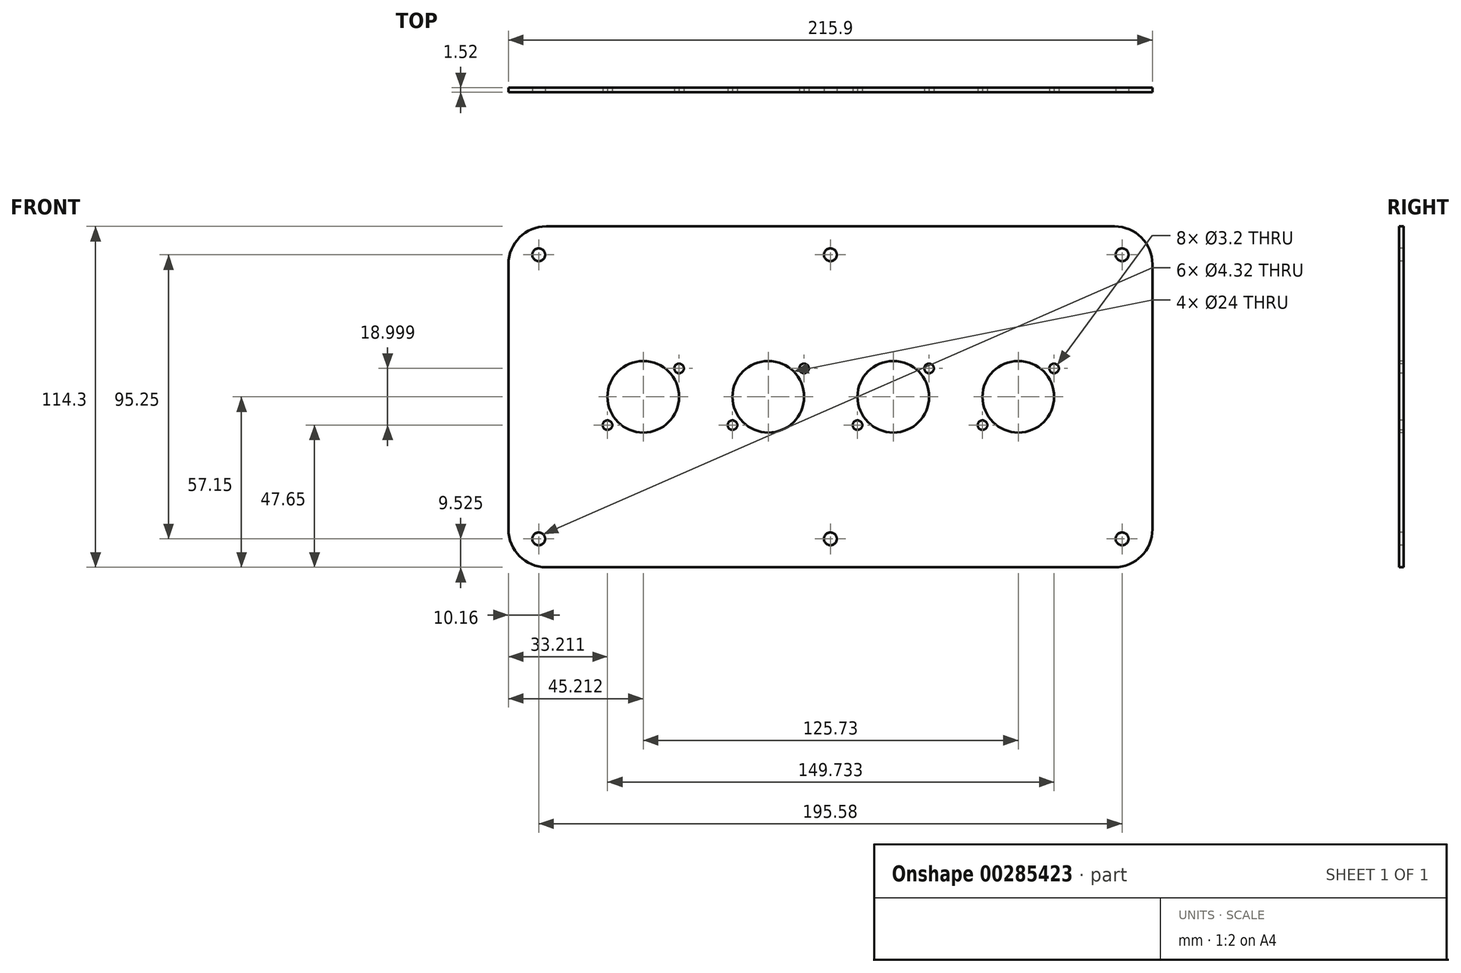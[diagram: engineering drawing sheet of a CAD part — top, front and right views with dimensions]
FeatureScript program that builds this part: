
annotation { "Feature Type Name" : "Feature", "Feature Type Description" : "" }
export const myFeature = defineFeature(function(context is Context, id is Id, definition is map)
    precondition{}
    {
        {
            var Q0;
            Q0=qCreatedBy(makeId("Front.planeOp"),FACE);
            var sketch = newSketch(context, id + "F0", { "sketchPlane" : qUnion([Q0])});
            skLineSegment(sketch, "E0.bottom", {"start": v(33.27, -22.23) * mm, "end": v(182.63, -22.23) * mm, "construction": true});
            skLineSegment(sketch, "E0.top", {"start": v(33.27, -92.08) * mm, "end": v(182.63, -92.08) * mm, "construction": true});
            skLineSegment(sketch, "E0.left", {"start": v(24.13, -31.37) * mm, "end": v(24.13, -82.93) * mm, "construction": true});
            skLineSegment(sketch, "E0.right", {"start": v(191.77, -31.37) * mm, "end": v(191.77, -82.93) * mm, "construction": true});
            skPoint(sketch, "E1.visualSharp", {"position": v(24.13, -22.23) * mm});
            skArc(sketch, "E1.filletArc", {"start": v(33.27, -22.23) * mm, "mid": v(26.8, -24.9) * mm, "end": v(24.13, -31.37) * mm, "construction": true});
            skPoint(sketch, "E2.visualSharp", {"position": v(191.77, -22.23) * mm});
            skArc(sketch, "E2.filletArc", {"start": v(191.77, -31.37) * mm, "mid": v(189.1, -24.9) * mm, "end": v(182.63, -22.22) * mm, "construction": true});
            skPoint(sketch, "E3.visualSharp", {"position": v(191.77, -92.08) * mm});
            skArc(sketch, "E3.filletArc", {"start": v(182.63, -92.08) * mm, "mid": v(189.1, -89.4) * mm, "end": v(191.77, -82.93) * mm, "construction": true});
            skPoint(sketch, "E4.visualSharp", {"position": v(24.13, -92.08) * mm});
            skArc(sketch, "E4.filletArc", {"start": v(24.13, -82.93) * mm, "mid": v(26.8, -89.4) * mm, "end": v(33.27, -92.07) * mm, "construction": true});
            skLineSegment(sketch, "E5.bottom", {"start": v(12.7, 0) * mm, "end": v(203.2, 0) * mm});
            skLineSegment(sketch, "E5.top", {"start": v(12.7, -114.3) * mm, "end": v(203.2, -114.3) * mm});
            skLineSegment(sketch, "E5.left", {"start": v(0, -12.7) * mm, "end": v(0, -101.6) * mm});
            skLineSegment(sketch, "E5.right", {"start": v(215.9, -12.7) * mm, "end": v(215.9, -101.6) * mm});
            skPoint(sketch, "E6.visualSharp", {"position": v(0, 0) * mm});
            skArc(sketch, "E6.filletArc", {"start": v(12.7, 0) * mm, "mid": v(3.72, -3.72) * mm, "end": v(0, -12.7) * mm});
            skPoint(sketch, "E7.visualSharp", {"position": v(215.9, 0) * mm});
            skArc(sketch, "E7.filletArc", {"start": v(215.9, -12.7) * mm, "mid": v(212.18, -3.72) * mm, "end": v(203.2, 0) * mm});
            skPoint(sketch, "E8.visualSharp", {"position": v(215.9, -114.3) * mm});
            skArc(sketch, "E8.filletArc", {"start": v(203.2, -114.3) * mm, "mid": v(212.18, -110.58) * mm, "end": v(215.9, -101.6) * mm});
            skPoint(sketch, "E9.visualSharp", {"position": v(0, -114.3) * mm});
            skArc(sketch, "E9.filletArc", {"start": v(0, -101.6) * mm, "mid": v(3.72, -110.58) * mm, "end": v(12.7, -114.3) * mm});
            skLineSegment(sketch, "E10", {"start": v(107.95, 0) * mm, "end": v(107.95, -114.3) * mm, "construction": true});
            skLineSegment(sketch, "E11", {"start": v(0, -57.15) * mm, "end": v(215.9, -57.15) * mm, "construction": true});
            skPoint(sketch, "E12", {"position": v(107.95, -22.23) * mm});
            skPoint(sketch, "E13", {"position": v(191.77, -57.15) * mm});
            skPoint(sketch, "E14", {"position": v(10.16, -9.52) * mm});
            skPoint(sketch, "E15", {"position": v(107.95, -9.52) * mm});
            skPoint(sketch, "E16", {"position": v(205.74, -9.52) * mm});
            skPoint(sketch, "E17", {"position": v(205.74, -104.78) * mm});
            skPoint(sketch, "E18", {"position": v(107.95, -104.78) * mm});
            skPoint(sketch, "E19", {"position": v(10.16, -104.78) * mm});
            skLineSegment(sketch, "E20", {"start": v(10.16, -9.52) * mm, "end": v(10.16, -104.78) * mm, "construction": true});
            skSolve(sketch);
        }
        {
            var Q0;
            Q0=makeQuery(id+"F0.imprint","IMPRINT",FACE,{"disambiguationData":[TD([[makeQuery(id+"F0.imprint","IMPRINT",EDGE,{"derivedFrom":sQuery(id+"F0.wireOp",EDGE,"E5.bottom")}),-1.0]])]});
            extrude(context, id + "F1", {"entities" : qUnion([Q0]), "depth" : 1.52 * mm});
        }
        {
            var Q0;
            Q0=makeQuery(id+"F1.opExtrude","CAP_FACE",FACE,{"disambiguationData":[OSD([sQuery(id+"F0.wireOp",EDGE,"E5.bottom"),sQuery(id+"F0.wireOp",EDGE,"E5.top"),sQuery(id+"F0.wireOp",EDGE,"E5.left"),sQuery(id+"F0.wireOp",EDGE,"E5.right"),sQuery(id+"F0.wireOp",EDGE,"E6.filletArc"),sQuery(id+"F0.wireOp",EDGE,"E7.filletArc"),sQuery(id+"F0.wireOp",EDGE,"E8.filletArc"),sQuery(id+"F0.wireOp",EDGE,"E9.filletArc")])],"isStart":false});
            var sketch = newSketch(context, id + "F2", { "sketchPlane" : qUnion([Q0])});
            skCircle(sketch, "E21", {"center": v(45.21, -57.15) * mm, "radius": 12 * mm});
            skCircle(sketch, "E22.MirrorC", {"center": v(33.21, -66.65) * mm, "radius": 1.6 * mm});
            skCircle(sketch, "E23.MirrorC", {"center": v(57.21, -47.65) * mm, "radius": 1.6 * mm});
            skLineSegment(sketch, "E24.bottom", {"start": v(29.72, -66.45) * mm, "end": v(29.72, -47.85) * mm, "construction": true});
            skLineSegment(sketch, "E24.top", {"start": v(60.7, -66.45) * mm, "end": v(60.7, -47.85) * mm, "construction": true});
            skLineSegment(sketch, "E24.left", {"start": v(33.22, -69.95) * mm, "end": v(57.2, -69.95) * mm, "construction": true});
            skLineSegment(sketch, "E24.right", {"start": v(33.22, -44.35) * mm, "end": v(57.2, -44.35) * mm, "construction": true});
            skPoint(sketch, "E25.visualSharp", {"position": v(29.72, -69.95) * mm});
            skArc(sketch, "E25.filletArc", {"start": v(29.72, -66.45) * mm, "mid": v(30.74, -68.93) * mm, "end": v(33.22, -69.95) * mm, "construction": true});
            skPoint(sketch, "E26.visualSharp", {"position": v(29.72, -44.35) * mm});
            skArc(sketch, "E26.filletArc", {"start": v(33.22, -44.35) * mm, "mid": v(30.74, -45.37) * mm, "end": v(29.72, -47.85) * mm, "construction": true});
            skPoint(sketch, "E27.visualSharp", {"position": v(60.7, -69.95) * mm});
            skArc(sketch, "E27.filletArc", {"start": v(57.2, -69.95) * mm, "mid": v(59.68, -68.93) * mm, "end": v(60.7, -66.45) * mm, "construction": true});
            skPoint(sketch, "E28.visualSharp", {"position": v(60.7, -44.35) * mm});
            skArc(sketch, "E28.filletArc", {"start": v(60.7, -47.85) * mm, "mid": v(59.68, -45.37) * mm, "end": v(57.2, -44.35) * mm, "construction": true});
            skLineSegment(sketch, "E29.bottom", {"start": v(64.81, -71.08) * mm, "end": v(64.81, -43.23) * mm, "construction": true});
            skLineSegment(sketch, "E29.top", {"start": v(25.61, -71.08) * mm, "end": v(25.61, -43.23) * mm, "construction": true});
            skLineSegment(sketch, "E29.left", {"start": v(61.64, -74.25) * mm, "end": v(28.79, -74.25) * mm, "construction": true});
            skLineSegment(sketch, "E29.right", {"start": v(61.64, -40.05) * mm, "end": v(28.79, -40.05) * mm, "construction": true});
            skCircle(sketch, "E30", {"center": v(45.21, -57.15) * mm, "radius": 11.8 * mm, "construction": true});
            skLineSegment(sketch, "E31", {"start": v(25.61, -57.15) * mm, "end": v(64.81, -57.15) * mm, "construction": true});
            skLineSegment(sketch, "E32", {"start": v(45.21, -40.05) * mm, "end": v(45.21, -74.25) * mm, "construction": true});
            skCircle(sketch, "E33", {"center": v(33.22, -66.65) * mm, "radius": 1.55 * mm, "construction": true});
            skCircle(sketch, "E34", {"center": v(57.2, -47.65) * mm, "radius": 1.55 * mm, "construction": true});
            skPoint(sketch, "E35.visualSharp", {"position": v(25.61, -74.25) * mm});
            skArc(sketch, "E35.filletArc", {"start": v(25.61, -71.08) * mm, "mid": v(26.54, -73.32) * mm, "end": v(28.79, -74.25) * mm, "construction": true});
            skPoint(sketch, "E36.visualSharp", {"position": v(25.61, -40.05) * mm});
            skArc(sketch, "E36.filletArc", {"start": v(28.79, -40.05) * mm, "mid": v(26.54, -40.98) * mm, "end": v(25.61, -43.23) * mm, "construction": true});
            skPoint(sketch, "E37.visualSharp", {"position": v(64.81, -40.05) * mm});
            skArc(sketch, "E37.filletArc", {"start": v(64.81, -43.23) * mm, "mid": v(63.88, -40.98) * mm, "end": v(61.64, -40.05) * mm, "construction": true});
            skPoint(sketch, "E38.visualSharp", {"position": v(64.81, -74.25) * mm});
            skArc(sketch, "E38.filletArc", {"start": v(61.64, -74.25) * mm, "mid": v(63.88, -73.32) * mm, "end": v(64.81, -71.08) * mm, "construction": true});
            skLineSegment(sketch, "E39", {"start": v(0, -57.15) * mm, "end": v(215.9, -57.15) * mm, "construction": true});
            skLineSegment(sketch, "E40.1.0.0", {"start": v(106.72, -71.08) * mm, "end": v(106.72, -43.23) * mm, "construction": true});
            skLineSegment(sketch, "E40.1.0.1", {"start": v(67.52, -71.08) * mm, "end": v(67.52, -43.23) * mm, "construction": true});
            skPoint(sketch, "E40.1.0.2", {"position": v(102.62, -44.35) * mm});
            skPoint(sketch, "E40.1.0.3", {"position": v(71.63, -69.95) * mm});
            skCircle(sketch, "E40.1.0.4", {"center": v(75.13, -66.65) * mm, "radius": 1.55 * mm, "construction": true});
            skCircle(sketch, "E40.1.0.5", {"center": v(99.12, -47.65) * mm, "radius": 1.6 * mm});
            skCircle(sketch, "E40.1.0.6", {"center": v(99.11, -47.65) * mm, "radius": 1.55 * mm, "construction": true});
            skPoint(sketch, "E40.1.0.7", {"position": v(106.72, -40.05) * mm});
            skPoint(sketch, "E40.1.0.8", {"position": v(102.62, -69.95) * mm});
            skPoint(sketch, "E40.1.0.9", {"position": v(67.52, -40.05) * mm});
            skCircle(sketch, "E40.1.0.10", {"center": v(87.12, -57.15) * mm, "radius": 11.8 * mm, "construction": true});
            skCircle(sketch, "E40.1.0.11", {"center": v(87.12, -57.15) * mm, "radius": 12 * mm});
            skLineSegment(sketch, "E40.1.0.12", {"start": v(75.13, -69.95) * mm, "end": v(99.12, -69.95) * mm, "construction": true});
            skLineSegment(sketch, "E40.1.0.13", {"start": v(103.55, -74.25) * mm, "end": v(70.7, -74.25) * mm, "construction": true});
            skLineSegment(sketch, "E40.1.0.14", {"start": v(75.13, -44.35) * mm, "end": v(99.12, -44.35) * mm, "construction": true});
            skLineSegment(sketch, "E40.1.0.15", {"start": v(103.55, -40.05) * mm, "end": v(70.7, -40.05) * mm, "construction": true});
            skLineSegment(sketch, "E40.1.0.16", {"start": v(71.63, -66.45) * mm, "end": v(71.63, -47.85) * mm, "construction": true});
            skLineSegment(sketch, "E40.1.0.17", {"start": v(102.62, -66.45) * mm, "end": v(102.62, -47.85) * mm, "construction": true});
            skPoint(sketch, "E40.1.0.18", {"position": v(67.52, -74.25) * mm});
            skPoint(sketch, "E40.1.0.19", {"position": v(106.72, -74.25) * mm});
            skCircle(sketch, "E40.1.0.20", {"center": v(75.12, -66.65) * mm, "radius": 1.6 * mm});
            skLineSegment(sketch, "E40.1.0.21", {"start": v(87.12, -40.05) * mm, "end": v(87.12, -74.25) * mm, "construction": true});
            skPoint(sketch, "E40.1.0.22", {"position": v(71.63, -44.35) * mm});
            skLineSegment(sketch, "E40.1.0.23", {"start": v(41.9, -57.15) * mm, "end": v(257.8, -57.15) * mm, "construction": true});
            skArc(sketch, "E40.1.0.24", {"start": v(103.55, -74.25) * mm, "mid": v(105.8, -73.32) * mm, "end": v(106.72, -71.08) * mm, "construction": true});
            skArc(sketch, "E40.1.0.25", {"start": v(102.62, -47.85) * mm, "mid": v(101.6, -45.37) * mm, "end": v(99.12, -44.35) * mm, "construction": true});
            skArc(sketch, "E40.1.0.26", {"start": v(99.12, -69.95) * mm, "mid": v(101.6, -68.93) * mm, "end": v(102.62, -66.45) * mm, "construction": true});
            skArc(sketch, "E40.1.0.27", {"start": v(75.13, -44.35) * mm, "mid": v(72.65, -45.37) * mm, "end": v(71.63, -47.85) * mm, "construction": true});
            skArc(sketch, "E40.1.0.28", {"start": v(67.52, -71.08) * mm, "mid": v(68.45, -73.32) * mm, "end": v(70.7, -74.25) * mm, "construction": true});
            skArc(sketch, "E40.1.0.29", {"start": v(71.63, -66.45) * mm, "mid": v(72.65, -68.93) * mm, "end": v(75.13, -69.95) * mm, "construction": true});
            skLineSegment(sketch, "E40.1.0.30", {"start": v(67.52, -57.15) * mm, "end": v(106.72, -57.15) * mm, "construction": true});
            skArc(sketch, "E40.1.0.31", {"start": v(106.72, -43.23) * mm, "mid": v(105.8, -40.98) * mm, "end": v(103.55, -40.05) * mm, "construction": true});
            skArc(sketch, "E40.1.0.32", {"start": v(70.7, -40.05) * mm, "mid": v(68.45, -40.98) * mm, "end": v(67.52, -43.23) * mm, "construction": true});
            skLineSegment(sketch, "E40.2.0.0", {"start": v(148.63, -71.08) * mm, "end": v(148.63, -43.23) * mm, "construction": true});
            skLineSegment(sketch, "E40.2.0.1", {"start": v(109.43, -71.08) * mm, "end": v(109.43, -43.23) * mm, "construction": true});
            skPoint(sketch, "E40.2.0.2", {"position": v(144.53, -44.35) * mm});
            skPoint(sketch, "E40.2.0.3", {"position": v(113.54, -69.95) * mm});
            skCircle(sketch, "E40.2.0.4", {"center": v(117.04, -66.65) * mm, "radius": 1.55 * mm, "construction": true});
            skCircle(sketch, "E40.2.0.5", {"center": v(141.03, -47.65) * mm, "radius": 1.6 * mm});
            skCircle(sketch, "E40.2.0.6", {"center": v(141.02, -47.65) * mm, "radius": 1.55 * mm, "construction": true});
            skPoint(sketch, "E40.2.0.7", {"position": v(148.63, -40.05) * mm});
            skPoint(sketch, "E40.2.0.8", {"position": v(144.53, -69.95) * mm});
            skPoint(sketch, "E40.2.0.9", {"position": v(109.43, -40.05) * mm});
            skCircle(sketch, "E40.2.0.10", {"center": v(129.03, -57.15) * mm, "radius": 11.8 * mm, "construction": true});
            skCircle(sketch, "E40.2.0.11", {"center": v(129.03, -57.15) * mm, "radius": 12 * mm});
            skLineSegment(sketch, "E40.2.0.12", {"start": v(117.04, -69.95) * mm, "end": v(141.03, -69.95) * mm, "construction": true});
            skLineSegment(sketch, "E40.2.0.13", {"start": v(145.46, -74.25) * mm, "end": v(112.6, -74.25) * mm, "construction": true});
            skLineSegment(sketch, "E40.2.0.14", {"start": v(117.04, -44.35) * mm, "end": v(141.03, -44.35) * mm, "construction": true});
            skLineSegment(sketch, "E40.2.0.15", {"start": v(145.46, -40.05) * mm, "end": v(112.6, -40.05) * mm, "construction": true});
            skLineSegment(sketch, "E40.2.0.16", {"start": v(113.54, -66.45) * mm, "end": v(113.54, -47.85) * mm, "construction": true});
            skLineSegment(sketch, "E40.2.0.17", {"start": v(144.53, -66.45) * mm, "end": v(144.53, -47.85) * mm, "construction": true});
            skPoint(sketch, "E40.2.0.18", {"position": v(109.43, -74.25) * mm});
            skPoint(sketch, "E40.2.0.19", {"position": v(148.63, -74.25) * mm});
            skCircle(sketch, "E40.2.0.20", {"center": v(117.03, -66.65) * mm, "radius": 1.6 * mm});
            skLineSegment(sketch, "E40.2.0.21", {"start": v(129.03, -40.05) * mm, "end": v(129.03, -74.25) * mm, "construction": true});
            skPoint(sketch, "E40.2.0.22", {"position": v(113.54, -44.35) * mm});
            skLineSegment(sketch, "E40.2.0.23", {"start": v(83.82, -57.15) * mm, "end": v(299.72, -57.15) * mm, "construction": true});
            skArc(sketch, "E40.2.0.24", {"start": v(145.46, -74.25) * mm, "mid": v(147.7, -73.32) * mm, "end": v(148.63, -71.08) * mm, "construction": true});
            skArc(sketch, "E40.2.0.25", {"start": v(144.53, -47.85) * mm, "mid": v(143.5, -45.37) * mm, "end": v(141.03, -44.35) * mm, "construction": true});
            skArc(sketch, "E40.2.0.26", {"start": v(141.03, -69.95) * mm, "mid": v(143.5, -68.93) * mm, "end": v(144.53, -66.45) * mm, "construction": true});
            skArc(sketch, "E40.2.0.27", {"start": v(117.04, -44.35) * mm, "mid": v(114.56, -45.37) * mm, "end": v(113.54, -47.85) * mm, "construction": true});
            skArc(sketch, "E40.2.0.28", {"start": v(109.43, -71.08) * mm, "mid": v(110.36, -73.32) * mm, "end": v(112.6, -74.25) * mm, "construction": true});
            skArc(sketch, "E40.2.0.29", {"start": v(113.54, -66.45) * mm, "mid": v(114.56, -68.93) * mm, "end": v(117.04, -69.95) * mm, "construction": true});
            skLineSegment(sketch, "E40.2.0.30", {"start": v(109.43, -57.15) * mm, "end": v(148.63, -57.15) * mm, "construction": true});
            skArc(sketch, "E40.2.0.31", {"start": v(148.63, -43.23) * mm, "mid": v(147.7, -40.98) * mm, "end": v(145.46, -40.05) * mm, "construction": true});
            skArc(sketch, "E40.2.0.32", {"start": v(112.6, -40.05) * mm, "mid": v(110.36, -40.98) * mm, "end": v(109.43, -43.23) * mm, "construction": true});
            skLineSegment(sketch, "E40.3.0.0", {"start": v(190.54, -71.08) * mm, "end": v(190.54, -43.23) * mm, "construction": true});
            skLineSegment(sketch, "E40.3.0.1", {"start": v(151.34, -71.08) * mm, "end": v(151.34, -43.23) * mm, "construction": true});
            skPoint(sketch, "E40.3.0.2", {"position": v(186.44, -44.35) * mm});
            skPoint(sketch, "E40.3.0.3", {"position": v(155.45, -69.95) * mm});
            skCircle(sketch, "E40.3.0.4", {"center": v(158.95, -66.65) * mm, "radius": 1.55 * mm, "construction": true});
            skCircle(sketch, "E40.3.0.5", {"center": v(182.94, -47.65) * mm, "radius": 1.6 * mm});
            skCircle(sketch, "E40.3.0.6", {"center": v(182.93, -47.65) * mm, "radius": 1.55 * mm, "construction": true});
            skPoint(sketch, "E40.3.0.7", {"position": v(190.54, -40.05) * mm});
            skPoint(sketch, "E40.3.0.8", {"position": v(186.44, -69.95) * mm});
            skPoint(sketch, "E40.3.0.9", {"position": v(151.34, -40.05) * mm});
            skCircle(sketch, "E40.3.0.10", {"center": v(170.94, -57.15) * mm, "radius": 11.8 * mm, "construction": true});
            skCircle(sketch, "E40.3.0.11", {"center": v(170.94, -57.15) * mm, "radius": 12 * mm});
            skLineSegment(sketch, "E40.3.0.12", {"start": v(158.95, -69.95) * mm, "end": v(182.94, -69.95) * mm, "construction": true});
            skLineSegment(sketch, "E40.3.0.13", {"start": v(187.37, -74.25) * mm, "end": v(154.52, -74.25) * mm, "construction": true});
            skLineSegment(sketch, "E40.3.0.14", {"start": v(158.95, -44.35) * mm, "end": v(182.94, -44.35) * mm, "construction": true});
            skLineSegment(sketch, "E40.3.0.15", {"start": v(187.37, -40.05) * mm, "end": v(154.52, -40.05) * mm, "construction": true});
            skLineSegment(sketch, "E40.3.0.16", {"start": v(155.45, -66.45) * mm, "end": v(155.45, -47.85) * mm, "construction": true});
            skLineSegment(sketch, "E40.3.0.17", {"start": v(186.44, -66.45) * mm, "end": v(186.44, -47.85) * mm, "construction": true});
            skPoint(sketch, "E40.3.0.18", {"position": v(151.34, -74.25) * mm});
            skPoint(sketch, "E40.3.0.19", {"position": v(190.54, -74.25) * mm});
            skCircle(sketch, "E40.3.0.20", {"center": v(158.94, -66.65) * mm, "radius": 1.6 * mm});
            skLineSegment(sketch, "E40.3.0.21", {"start": v(170.94, -40.05) * mm, "end": v(170.94, -74.25) * mm, "construction": true});
            skPoint(sketch, "E40.3.0.22", {"position": v(155.45, -44.35) * mm});
            skLineSegment(sketch, "E40.3.0.23", {"start": v(125.73, -57.15) * mm, "end": v(341.63, -57.15) * mm, "construction": true});
            skArc(sketch, "E40.3.0.24", {"start": v(187.37, -74.25) * mm, "mid": v(189.61, -73.32) * mm, "end": v(190.54, -71.08) * mm, "construction": true});
            skArc(sketch, "E40.3.0.25", {"start": v(186.44, -47.85) * mm, "mid": v(185.41, -45.37) * mm, "end": v(182.94, -44.35) * mm, "construction": true});
            skArc(sketch, "E40.3.0.26", {"start": v(182.94, -69.95) * mm, "mid": v(185.41, -68.93) * mm, "end": v(186.44, -66.45) * mm, "construction": true});
            skArc(sketch, "E40.3.0.27", {"start": v(158.95, -44.35) * mm, "mid": v(156.47, -45.37) * mm, "end": v(155.45, -47.85) * mm, "construction": true});
            skArc(sketch, "E40.3.0.28", {"start": v(151.34, -71.08) * mm, "mid": v(152.27, -73.32) * mm, "end": v(154.52, -74.25) * mm, "construction": true});
            skArc(sketch, "E40.3.0.29", {"start": v(155.45, -66.45) * mm, "mid": v(156.47, -68.93) * mm, "end": v(158.95, -69.95) * mm, "construction": true});
            skLineSegment(sketch, "E40.3.0.30", {"start": v(151.34, -57.15) * mm, "end": v(190.54, -57.15) * mm, "construction": true});
            skArc(sketch, "E40.3.0.31", {"start": v(190.54, -43.23) * mm, "mid": v(189.61, -40.98) * mm, "end": v(187.37, -40.05) * mm, "construction": true});
            skArc(sketch, "E40.3.0.32", {"start": v(154.52, -40.05) * mm, "mid": v(152.27, -40.98) * mm, "end": v(151.34, -43.23) * mm, "construction": true});
            skLineSegment(sketch, "E40.direction1", {"start": v(0, -57.15) * mm, "end": v(41.91, -57.15) * mm, "construction": true});
            skSolve(sketch);
        }
        {
            var Q0;
            Q0=qSketchRegion(id+"F2",true);
            extrude(context, id + "F3", {"entities" : qUnion([Q0]), "operationType" : NewBodyOperationType.REMOVE, "endBound" : BoundingType.THROUGH_ALL, "oppositeDirection" : true, "depth" : 25.4 * mm});
        }
        {
            var Q0;
            Q0=makeQuery(id+"F1.opExtrude","CAP_FACE",FACE,{"disambiguationData":[OSD([sQuery(id+"F0.wireOp",EDGE,"E5.bottom"),sQuery(id+"F0.wireOp",EDGE,"E5.top"),sQuery(id+"F0.wireOp",EDGE,"E5.left"),sQuery(id+"F0.wireOp",EDGE,"E5.right"),sQuery(id+"F0.wireOp",EDGE,"E6.filletArc"),sQuery(id+"F0.wireOp",EDGE,"E7.filletArc"),sQuery(id+"F0.wireOp",EDGE,"E8.filletArc"),sQuery(id+"F0.wireOp",EDGE,"E9.filletArc")])],"isStart":false});
            var sketch = newSketch(context, id + "F4", { "sketchPlane" : qUnion([Q0])});
            skPoint(sketch, "E41", {"position": v(10.16, -9.53) * mm});
            skPoint(sketch, "E42", {"position": v(107.95, -9.53) * mm});
            skPoint(sketch, "E43", {"position": v(205.74, -9.53) * mm});
            skPoint(sketch, "E44", {"position": v(205.74, -104.78) * mm});
            skPoint(sketch, "E45", {"position": v(107.95, -104.78) * mm});
            skPoint(sketch, "E46", {"position": v(10.16, -104.78) * mm});
            skSolve(sketch);
        }
        {
            var Q0;
            Q0=sQuery(id+"F4.wireOp",VERTEX,"E41");
            var Q1;
            Q1=sQuery(id+"F4.wireOp",VERTEX,"E42");
            var Q2;
            Q2=sQuery(id+"F4.wireOp",VERTEX,"E43");
            var Q3;
            Q3=sQuery(id+"F4.wireOp",VERTEX,"E44");
            var Q4;
            Q4=sQuery(id+"F4.wireOp",VERTEX,"E45");
            var Q5;
            Q5=sQuery(id+"F4.wireOp",VERTEX,"E46");
            var Q6;
            Q6=makeQuery(id+"F1.opExtrude","SWEPT_BODY",BODY,{"disambiguationData":[OSD([sQuery(id+"F0.wireOp",EDGE,"E5.bottom"),sQuery(id+"F0.wireOp",EDGE,"E5.top"),sQuery(id+"F0.wireOp",EDGE,"E5.left"),sQuery(id+"F0.wireOp",EDGE,"E5.right"),sQuery(id+"F0.wireOp",EDGE,"E6.filletArc"),sQuery(id+"F0.wireOp",EDGE,"E7.filletArc"),sQuery(id+"F0.wireOp",EDGE,"E8.filletArc"),sQuery(id+"F0.wireOp",EDGE,"E9.filletArc")])]});
            hole(context, id + "F5", {"style" : HoleStyle.SIMPLE, "endStyle" : HoleEndStyle.THROUGH, "standardTappedOrClearance" : lookupTablePath({ "standard" : "ANSI", "fit" : "Close", "size" : "#8", "type" : "Clearance" }), "standardBlindInLast" : lookupTablePath({ "fit" : "Close", "standard" : "ANSI", "size" : "#8", "type" : "Clearance" }), "holeDiameter" : 4.32 * mm, "isTappedThrough" : true, "tappedDepth" : 2.4 * mm, "tapClearance" : 3, "startFromSketch" : true, "locations" : qUnion([Q0, Q1, Q2, Q3, Q4, Q5]), "scope" : qUnion([Q6])});
        }
    });
